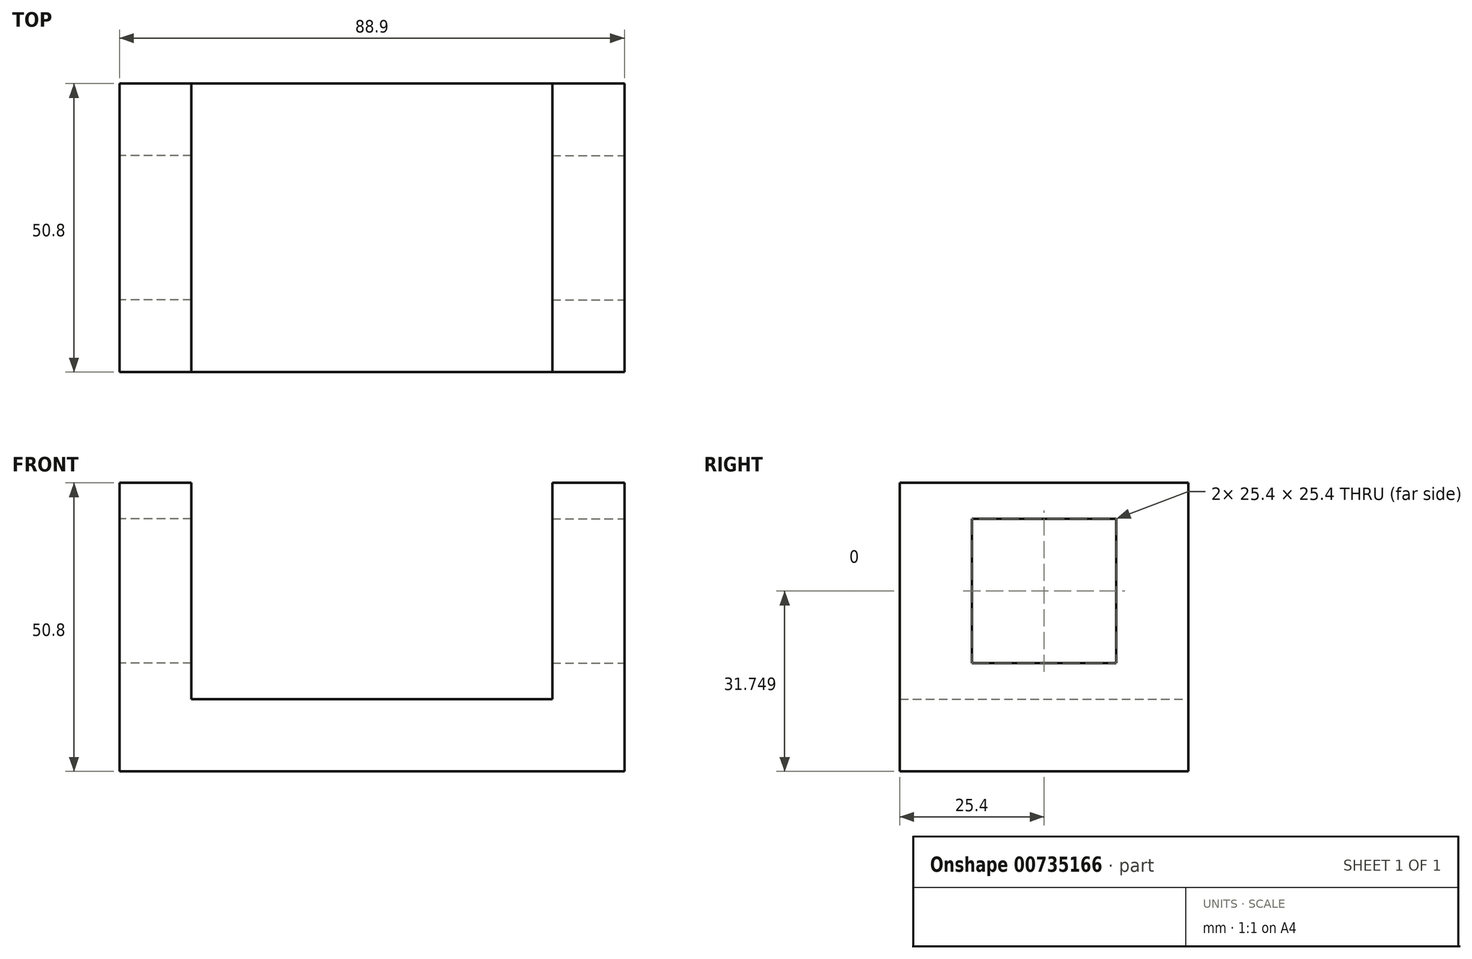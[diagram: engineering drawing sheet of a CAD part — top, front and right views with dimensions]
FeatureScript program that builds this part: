
annotation { "Feature Type Name" : "Feature", "Feature Type Description" : "" }
export const myFeature = defineFeature(function(context is Context, id is Id, definition is map)
    precondition{}
    {
        {
            var Q0;
            Q0=qCreatedBy(makeId("Front.planeOp"),FACE);
            var sketch = newSketch(context, id + "F0", { "sketchPlane" : qUnion([Q0])});
            skLineSegment(sketch, "E0", {"start": v(-12.7, 24.17) * mm, "end": v(-12.7, -13.93) * mm});
            skLineSegment(sketch, "E1", {"start": v(-12.7, -13.93) * mm, "end": v(-76.2, -13.93) * mm});
            skLineSegment(sketch, "E2", {"start": v(-76.2, -13.93) * mm, "end": v(-76.2, 24.17) * mm});
            skLineSegment(sketch, "E3", {"start": v(-76.2, 24.17) * mm, "end": v(-88.9, 24.17) * mm});
            skLineSegment(sketch, "E4", {"start": v(-88.9, 24.17) * mm, "end": v(-88.9, -26.63) * mm});
            skLineSegment(sketch, "E5", {"start": v(-88.9, -26.63) * mm, "end": v(0, -26.63) * mm});
            skLineSegment(sketch, "E6", {"start": v(-12.7, 24.17) * mm, "end": v(0, 24.17) * mm});
            skLineSegment(sketch, "E7", {"start": v(0, 24.17) * mm, "end": v(0, -26.63) * mm});
            skSolve(sketch);
        }
        {
            var Q0;
            Q0 = qSketchRegion(id + "F0", true);
            extrude(context, id + "F1", {"entities" : qUnion([Q0]), "depth" : 50.8 * mm, "offsetDistance" : 25.4 * mm});
        }
        {
            var Q0;
            Q0=makeQuery(id+"F1.opExtrude","SWEPT_FACE",FACE,{"disambiguationData":[OSD([sQuery(id+"F0.wireOp",EDGE,"E7")])]});
            var sketch = newSketch(context, id + "F2", { "sketchPlane" : qUnion([Q0])});
            skLineSegment(sketch, "E8.bottom", {"start": v(-38.1, 17.82) * mm, "end": v(-12.7, 17.82) * mm});
            skLineSegment(sketch, "E8.top", {"start": v(-38.1, -7.58) * mm, "end": v(-12.7, -7.58) * mm});
            skLineSegment(sketch, "E8.left", {"start": v(-38.1, 17.82) * mm, "end": v(-38.1, -7.58) * mm});
            skLineSegment(sketch, "E8.right", {"start": v(-12.7, 17.82) * mm, "end": v(-12.7, -7.58) * mm});
            skLineSegment(sketch, "E9", {"start": v(-27.88, -7.58) * mm, "end": v(-27.88, -26.63) * mm});
            skLineSegment(sketch, "E10", {"start": v(-12.7, 5.12) * mm, "end": v(0, 5.12) * mm});
            skSolve(sketch);
        }
        {
            var Q0;
            {var subQ5=sQuery(id+"F2.wireOp",EDGE,"E8.bottom");Q0=makeQuery(id+"F2.imprint","IMPRINT",FACE,{"disambiguationData":[TD([[makeQuery(id+"F2.imprint","IMPRINT",EDGE,{"derivedFrom":subQ5}),-1.0]])]});}
            extrude(context, id + "F3", {"entities" : qUnion([Q0]), "operationType" : NewBodyOperationType.REMOVE, "oppositeDirection" : true, "depth" : 12.7 * mm, "offsetDistance" : 25.4 * mm});
        }
        {
            var Q0;
            Q0=makeQuery(id+"F1.opExtrude","SWEPT_FACE",FACE,{"disambiguationData":[OSD([sQuery(id+"F0.wireOp",EDGE,"E4")])]});
            var sketch = newSketch(context, id + "F4", { "sketchPlane" : qUnion([Q0])});
            skLineSegment(sketch, "E11", {"start": v(12.7, 17.82) * mm, "end": v(38.1, 17.82) * mm});
            skLineSegment(sketch, "E12", {"start": v(38.1, 17.82) * mm, "end": v(38.1, -7.58) * mm});
            skLineSegment(sketch, "E13", {"start": v(38.1, -7.58) * mm, "end": v(12.7, -7.58) * mm});
            skLineSegment(sketch, "E14", {"start": v(12.7, -7.58) * mm, "end": v(12.7, 17.82) * mm});
            skLineSegment(sketch, "E15", {"start": v(25.4, -7.58) * mm, "end": v(25.4, -26.63) * mm});
            skPoint(sketch, "E15.startSnap0", {"position": v(25.4, -26.63) * mm});
            skLineSegment(sketch, "E16", {"start": v(38.1, 5.12) * mm, "end": v(50.8, 5.12) * mm});
            skSolve(sketch);
        }
        {
            var Q0;
            {var subQ5=sQuery(id+"F4.wireOp",EDGE,"E11");Q0=makeQuery(id+"F4.imprint","IMPRINT",FACE,{"disambiguationData":[TD([[makeQuery(id+"F4.imprint","IMPRINT",EDGE,{"derivedFrom":subQ5}),-1.0]])]});}
            extrude(context, id + "F5", {"entities" : qUnion([Q0]), "operationType" : NewBodyOperationType.REMOVE, "oppositeDirection" : true, "depth" : 12.7 * mm, "offsetDistance" : 25.4 * mm});
        }
    });
